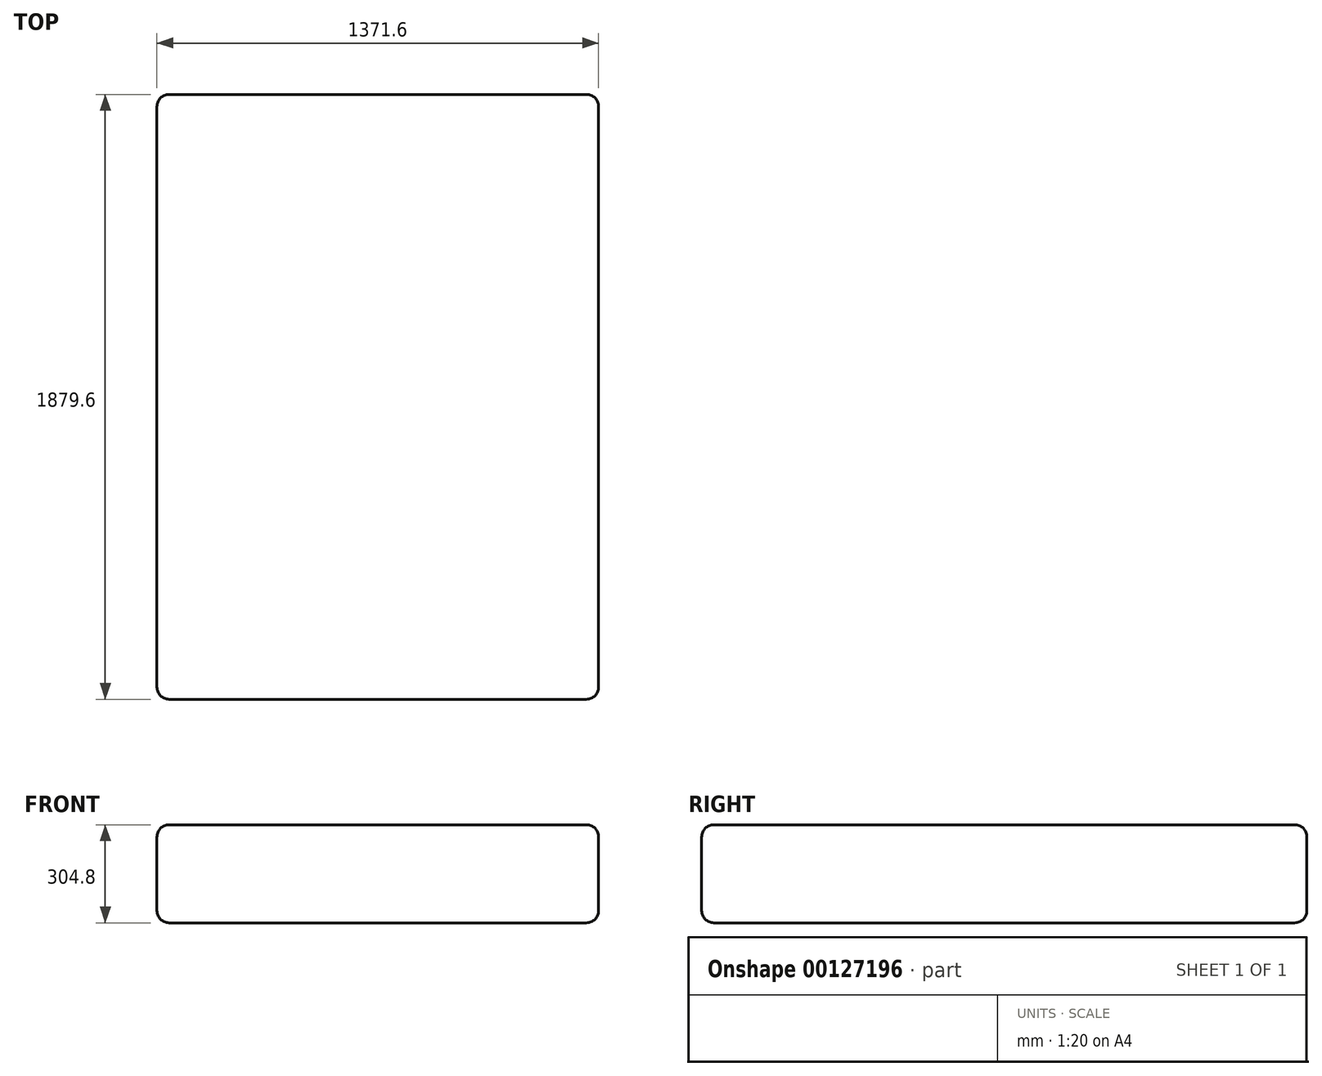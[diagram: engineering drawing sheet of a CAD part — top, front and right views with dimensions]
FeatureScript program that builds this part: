
annotation { "Feature Type Name" : "Feature", "Feature Type Description" : "" }
export const myFeature = defineFeature(function(context is Context, id is Id, definition is map)
    precondition{}
    {
        {
            var Q0;
            Q0=qCreatedBy(makeId("Front.planeOp"),FACE);
            var sketch = newSketch(context, id + "F0", { "sketchPlane" : qUnion([Q0])});
            skLineSegment(sketch, "E0.bottom", {"start": v(647.7, -152.4) * mm, "end": v(-647.7, -152.4) * mm});
            skLineSegment(sketch, "E0.top", {"start": v(647.7, 152.4) * mm, "end": v(-647.7, 152.4) * mm});
            skLineSegment(sketch, "E0.left", {"start": v(685.8, -114.3) * mm, "end": v(685.8, 114.3) * mm});
            skLineSegment(sketch, "E0.right", {"start": v(-685.8, -114.3) * mm, "end": v(-685.8, 114.3) * mm});
            skPoint(sketch, "E0.middle", {"position": v(0, 0) * mm});
            skPoint(sketch, "E1.visualSharp", {"position": v(-685.8, 152.4) * mm});
            skArc(sketch, "E1.filletArc", {"start": v(-647.7, 152.4) * mm, "mid": v(-674.64, 141.24) * mm, "end": v(-685.8, 114.3) * mm});
            skPoint(sketch, "E2.visualSharp", {"position": v(-685.8, -152.4) * mm});
            skArc(sketch, "E2.filletArc", {"start": v(-685.8, -114.3) * mm, "mid": v(-674.64, -141.24) * mm, "end": v(-647.7, -152.4) * mm});
            skPoint(sketch, "E3.visualSharp", {"position": v(685.8, -152.4) * mm});
            skArc(sketch, "E3.filletArc", {"start": v(647.7, -152.4) * mm, "mid": v(674.64, -141.24) * mm, "end": v(685.8, -114.3) * mm});
            skPoint(sketch, "E4.visualSharp", {"position": v(685.8, 152.4) * mm});
            skArc(sketch, "E4.filletArc", {"start": v(685.8, 114.3) * mm, "mid": v(674.64, 141.24) * mm, "end": v(647.7, 152.4) * mm});
            skSolve(sketch);
        }
        {
            var Q0;
            Q0=qSketchRegion(id+"F0",true);
            extrude(context, id + "F1", {"entities" : qUnion([Q0]), "depth" : 1879.6 * mm, "offsetDistance" : 25.4 * mm});
        }
        {
            var Q0;
            Q0=makeQuery(id+"F1.opExtrude","CAP_EDGE",EDGE,{"disambiguationData":[OSD([sQuery(id+"F0.wireOp",EDGE,"E0.left")])],"isStart":false});
            var Q1;
            Q1=makeQuery(id+"F1.opExtrude","SWEPT_EDGE",EDGE,{"disambiguationData":[OSD([sQuery(id+"F0.wireOp",EDGE,"E0.top"),sQuery(id+"F0.wireOp",EDGE,"E4.filletArc")])]});
            var Q2;
            Q2=makeQuery(id+"F1.opExtrude","CAP_EDGE",EDGE,{"disambiguationData":[OSD([sQuery(id+"F0.wireOp",EDGE,"E0.left")])],"isStart":true});
            fillet(context, id + "F2", {"entities" : qUnion([Q0, Q1, Q2]), "radius" : 38.1 * mm, "tangentPropagation" : true, "allowEdgeOverflow" : false});
        }
    });
